# Revit family: Gutter-Cove-Section
name_source: partatom
category: Detail Items
revit_build: Autodesk Revit Architecture 2012 (Build: 20110210_1515)
units: mm (PartAtom-declared; Revit-internal decimal feet)

## types (8) — shared parameters

## per-type parameters (varying)
| type | Base | Depth | Gutter Height | Keynote | Lip Depth | Lip Height | Overflow (1/2"min) |
| 6" x 6" | 0' - 3" | 0' - 6" | 0' - 6" | 07 62 00.H30 | 0' - 0 3/4" | 0' - 0 3/4" | 0' - 0 1/2" |
| 6" x 4" | 0' - 4" | 0' - 6" | 0' - 4" | 07 62 00.H28 | 0' - 0 1/2" | 0' - 0 1/2" | 0' - 0 1/2" |
| 6" x 5" | 0' - 3" | 0' - 6" | 0' - 5" | 07 62 00.H29 | 0' - 0 1/2" | 0' - 0 1/2" | 0' - 0 1/2" |
| 4" x 5" | 0' - 1 1/2" | 0' - 4" | 0' - 5" | 07 62 00.H27 | 0' - 0 1/2" | 0' - 0 1/2" | 0' - 0 1/2" |
| 4" x 4" | 0' - 2" | 0' - 4" | 0' - 4" | 07 62 00.H26 | 0' - 0 1/2" | 0' - 0 1/2" | 0' - 0 1/2" |
| 8" x 6" | 0' - 5" | 0' - 8" | 0' - 6" | 07 62 00.H31 | 0' - 0 1/2" | 0' - 0 3/4" | 0' - 0 1/2" |
| 8" x 8" | 0' - 4" | 0' - 8" | 0' - 8" | 07 62 00.H32 | 0' - 1" | 0' - 1" | 0' - 0 3/4" |
| 10" x 10" | 0' - 5" | 0' - 10" | 0' - 10" | 07 62 00.H33 | 0' - 1 1/2" | 0' - 1 1/2" | 0' - 1" |
